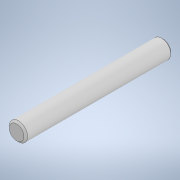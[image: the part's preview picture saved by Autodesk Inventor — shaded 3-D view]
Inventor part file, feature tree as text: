
AUTODESK INVENTOR PART (.ipt)
format: ipt  version: 2022 (Build 260153000, 153)  size: 96,768 bytes
history: native  units: mm
features: extrude x1, chamfer x1, sketch x1
ambient origin geometry x8: Origin, YZ Plane, XZ Plane, XY Plane, X Axis, Y Axis, Z Axis, Center Point
bodies: Solid1 (feature_tree)
feature tree (3):
  extrude  "Extrusion1"  Depth=80.0mm TaperAngle=0.0deg
  chamfer  "Chamfer1"  Distance=1.0mm Angle=45.0deg
  sketch  "Sketch1"  dims[d0=10.0mm d1=80.0mm d2=0.0mm d3=1.0mm d4=2.0mm d5=45.0deg]
